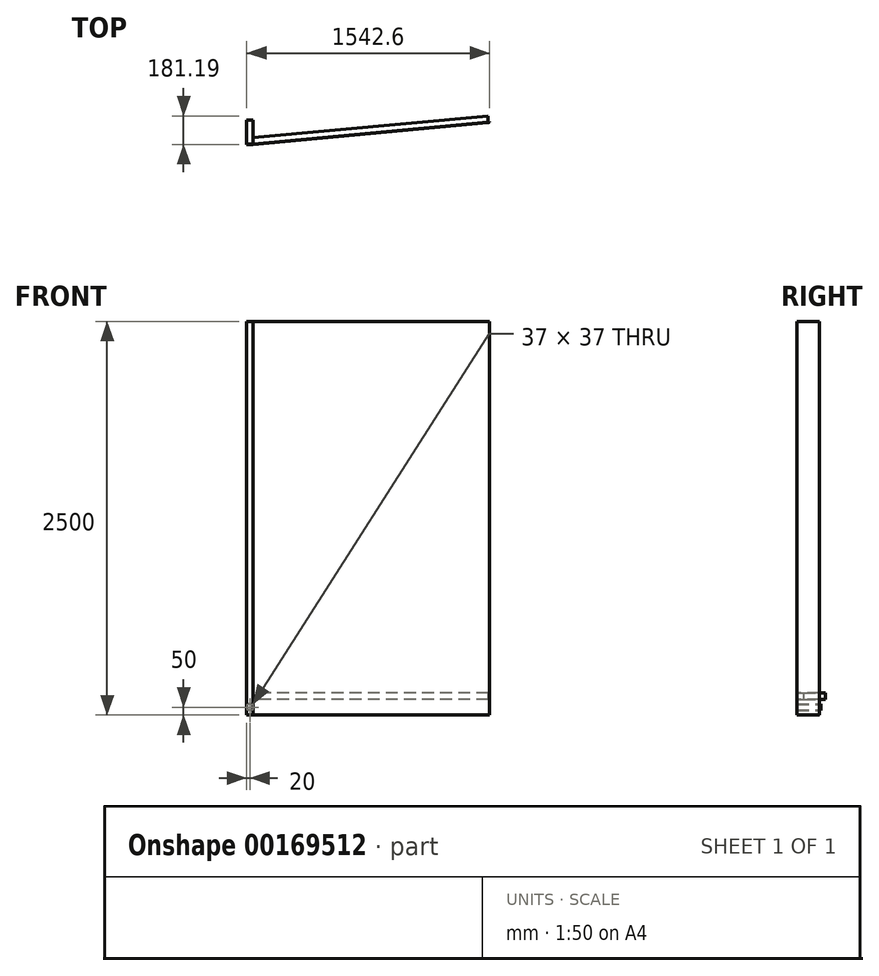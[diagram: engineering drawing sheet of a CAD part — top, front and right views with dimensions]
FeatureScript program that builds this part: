
annotation { "Feature Type Name" : "Feature", "Feature Type Description" : "" }
export const myFeature = defineFeature(function(context is Context, id is Id, definition is map)
    precondition{}
    {
        {
            var Q0;
            Q0=qCreatedBy(makeId("Front.planeOp"),FACE);
            var sketch = newSketch(context, id + "F0", { "sketchPlane" : qUnion([Q0])});
            skLineSegment(sketch, "E0.bottom", {"start": v(20, 20) * mm, "end": v(-20, 20) * mm});
            skLineSegment(sketch, "E0.top", {"start": v(20, -20) * mm, "end": v(-20, -20) * mm});
            skLineSegment(sketch, "E0.left", {"start": v(20, 20) * mm, "end": v(20, -20) * mm});
            skLineSegment(sketch, "E0.right", {"start": v(-20, 20) * mm, "end": v(-20, -20) * mm});
            skPoint(sketch, "E0.middle", {"position": v(0, 0) * mm});
            skLineSegment(sketch, "E1.bottom", {"start": v(18.5, 18.5) * mm, "end": v(-18.5, 18.5) * mm});
            skLineSegment(sketch, "E1.top", {"start": v(18.5, -18.5) * mm, "end": v(-18.5, -18.5) * mm});
            skLineSegment(sketch, "E1.left", {"start": v(18.5, 18.5) * mm, "end": v(18.5, -18.5) * mm});
            skLineSegment(sketch, "E1.right", {"start": v(-18.5, 18.5) * mm, "end": v(-18.5, -18.5) * mm});
            skSolve(sketch);
        }
        {
            var Q0;
            Q0 = qSketchRegion(id + "F0", true);
            extrude(context, id + "F1", {"entities" : qUnion([Q0]), "depth" : 150 * mm});
        }
        {
            var Q0;
            Q0=qCreatedBy(makeId("Top.planeOp"),FACE);
            cPlane(context, id + "F2", {"entities" : qUnion([Q0]), "cplaneType" : CPlaneType.OFFSET, "offset" : 50 * mm, "width" : 150 * mm, "height" : 150 * mm});
        }
        {
            var Q0;
            Q0=qCreatedBy(id+"F2.planeOp",FACE);
            var sketch = newSketch(context, id + "F3", { "sketchPlane" : qUnion([Q0])});
            skLineSegment(sketch, "E2", {"start": v(0, 0) * mm, "end": v(1200, 0) * mm});
            skPoint(sketch, "E3", {"position": v(20, -150) * mm});
            skPoint(sketch, "E4", {"position": v(0, 0) * mm});
            skLineSegment(sketch, "E5", {"start": v(20, -150) * mm, "end": v(20, -110) * mm});
            skLineSegment(sketch, "E6", {"start": v(20, -110) * mm, "end": v(1513.62, 28.2) * mm});
            skLineSegment(sketch, "E7", {"start": v(1513.62, 28.2) * mm, "end": v(1513.62, -11.8) * mm});
            skLineSegment(sketch, "E8", {"start": v(1513.62, -11.8) * mm, "end": v(20, -150) * mm});
            skSolve(sketch);
        }
        {
            var Q0;
            Q0 = qSketchRegion(id + "F3", true);
            extrude(context, id + "F4", {"entities" : qUnion([Q0]), "depth" : 40 * mm});
        }
        {
            var Q0;
            Q0=qCreatedBy(makeId("Top.planeOp"),FACE);
            cPlane(context, id + "F5", {"entities" : qUnion([Q0]), "cplaneType" : CPlaneType.OFFSET, "offset" : 50 * mm, "oppositeDirection" : true, "width" : 150 * mm, "height" : 150 * mm});
        }
        {
            var Q0;
            Q0=qCreatedBy(id+"F5.planeOp",FACE);
            var sketch = newSketch(context, id + "F6", { "sketchPlane" : qUnion([Q0])});
            skLineSegment(sketch, "E9.0", {"start": v(20.14, -153) * mm, "end": v(-20, -153) * mm});
            skLineSegment(sketch, "E9.1", {"start": v(1512.97, -14.88) * mm, "end": v(20.14, -153) * mm});
            skLineSegment(sketch, "E10", {"start": v(-20, -153) * mm, "end": v(-20, -150) * mm});
            skLineSegment(sketch, "E11.0", {"start": v(20, -150) * mm, "end": v(-20, -150) * mm});
            skLineSegment(sketch, "E12.0", {"start": v(1512.89, -11.87) * mm, "end": v(20, -150) * mm});
            skLineSegment(sketch, "E13", {"start": v(1514.73, -14.38) * mm, "end": v(1522.57, -10.47) * mm});
            skLineSegment(sketch, "E14", {"start": v(1514.3, -11.53) * mm, "end": v(1522.6, -8.16) * mm});
            skLineSegment(sketch, "E15", {"start": v(1522.57, -10.47) * mm, "end": v(1522.6, -8.16) * mm});
            skPoint(sketch, "E16.visualSharp", {"position": v(1513.62, -11.8) * mm});
            skArc(sketch, "E16.filletArc", {"start": v(1512.89, -11.87) * mm, "mid": v(1513.6, -11.75) * mm, "end": v(1514.3, -11.53) * mm});
            skPoint(sketch, "E17.visualSharp", {"position": v(1513.9, -14.8) * mm});
            skArc(sketch, "E17.filletArc", {"start": v(1512.97, -14.88) * mm, "mid": v(1513.87, -14.7) * mm, "end": v(1514.73, -14.38) * mm});
            skSolve(sketch);
        }
        {
            var Q0;
            Q0 = qSketchRegion(id + "F6", true);
            extrude(context, id + "F7", {"entities" : qUnion([Q0]), "depth" : 2500 * mm});
        }
    });
